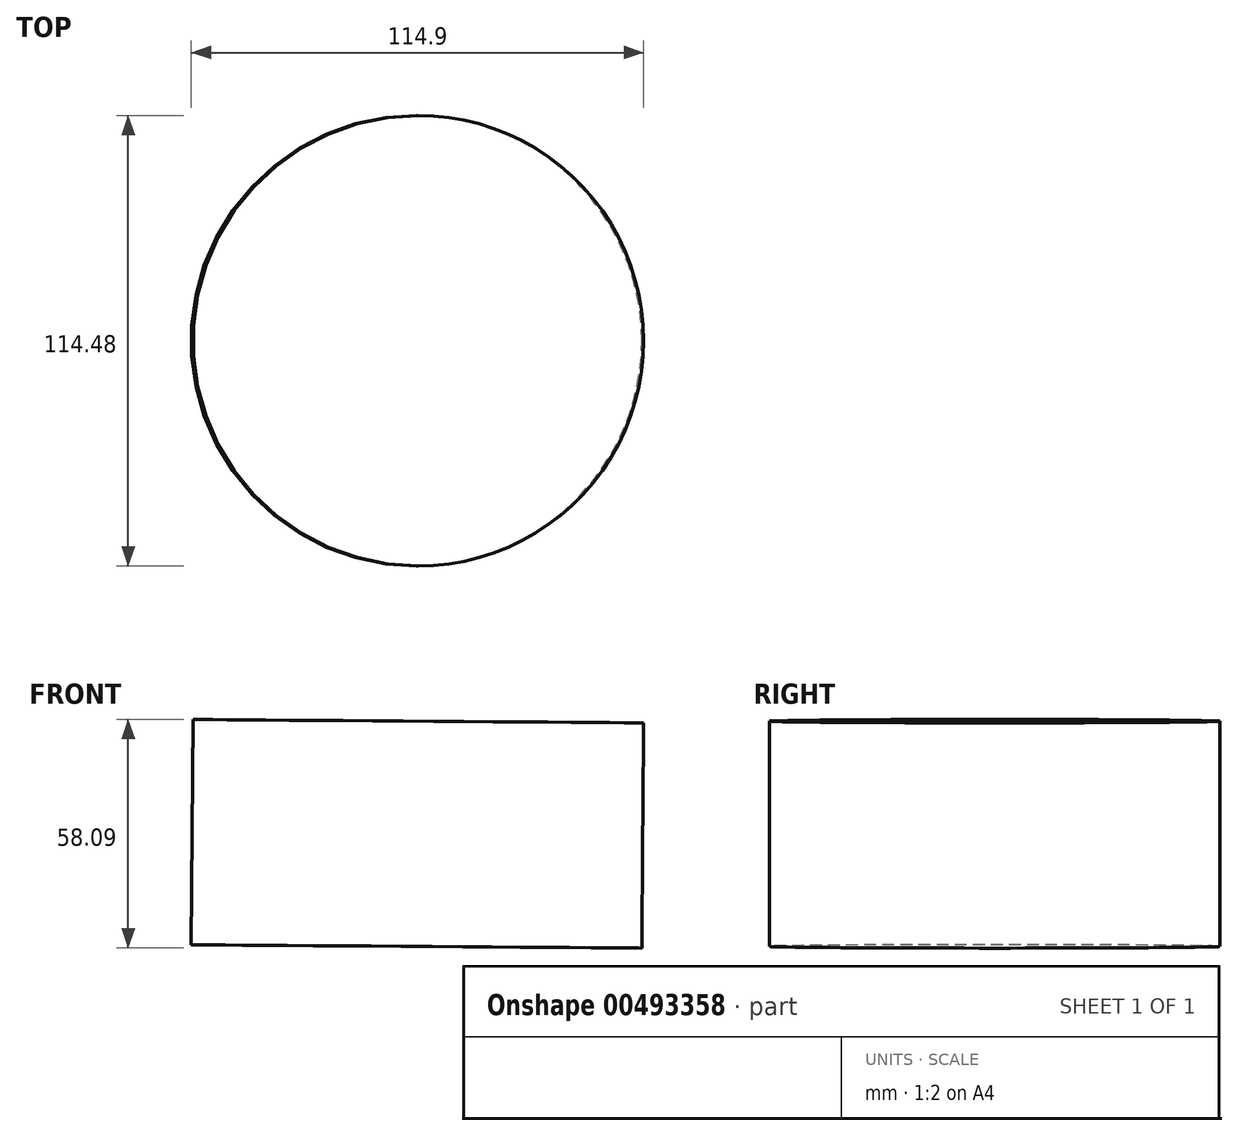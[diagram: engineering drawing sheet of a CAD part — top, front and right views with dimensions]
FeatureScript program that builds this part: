
annotation { "Feature Type Name" : "Feature", "Feature Type Description" : "" }
export const myFeature = defineFeature(function(context is Context, id is Id, definition is map)
    precondition{}
    {
        {
            var Q0;
            Q0=qCreatedBy(makeId("Front.planeOp"),FACE);
            var sketch = newSketch(context, id + "F0", { "sketchPlane" : qUnion([Q0])});
            skCircle(sketch, "E0.cCircle", {"center": v(0, 0) * mm, "radius": 40.47 * mm, "construction": true});
            skLineSegment(sketch, "E0.0", {"start": v(-28.4, 28.83) * mm, "end": v(28.83, 28.4) * mm});
            skLineSegment(sketch, "E0.1", {"start": v(28.83, 28.4) * mm, "end": v(28.4, -28.83) * mm});
            skLineSegment(sketch, "E0.2", {"start": v(28.4, -28.83) * mm, "end": v(-28.83, -28.4) * mm});
            skLineSegment(sketch, "E0.3", {"start": v(-28.83, -28.4) * mm, "end": v(-28.4, 28.83) * mm});
            skSolve(sketch);
        }
        {
            var Q0;
            Q0=makeQuery(id+"F0.imprint","IMPRINT",FACE,{"disambiguationData":[TD([[makeQuery(id+"F0.imprint","IMPRINT",EDGE,{"derivedFrom":sQuery(id+"F0.wireOp",EDGE,"E0.0")}),-1.0]])]});
            var Q1;
            Q1=sQuery(id+"F0.wireOp",EDGE,"E0.1");
            revolve(context, id + "F1", {"entities" : qUnion([Q0]), "axis" : qUnion([Q1]), "revolveType" : RevolveType.FULL});
        }
    });
